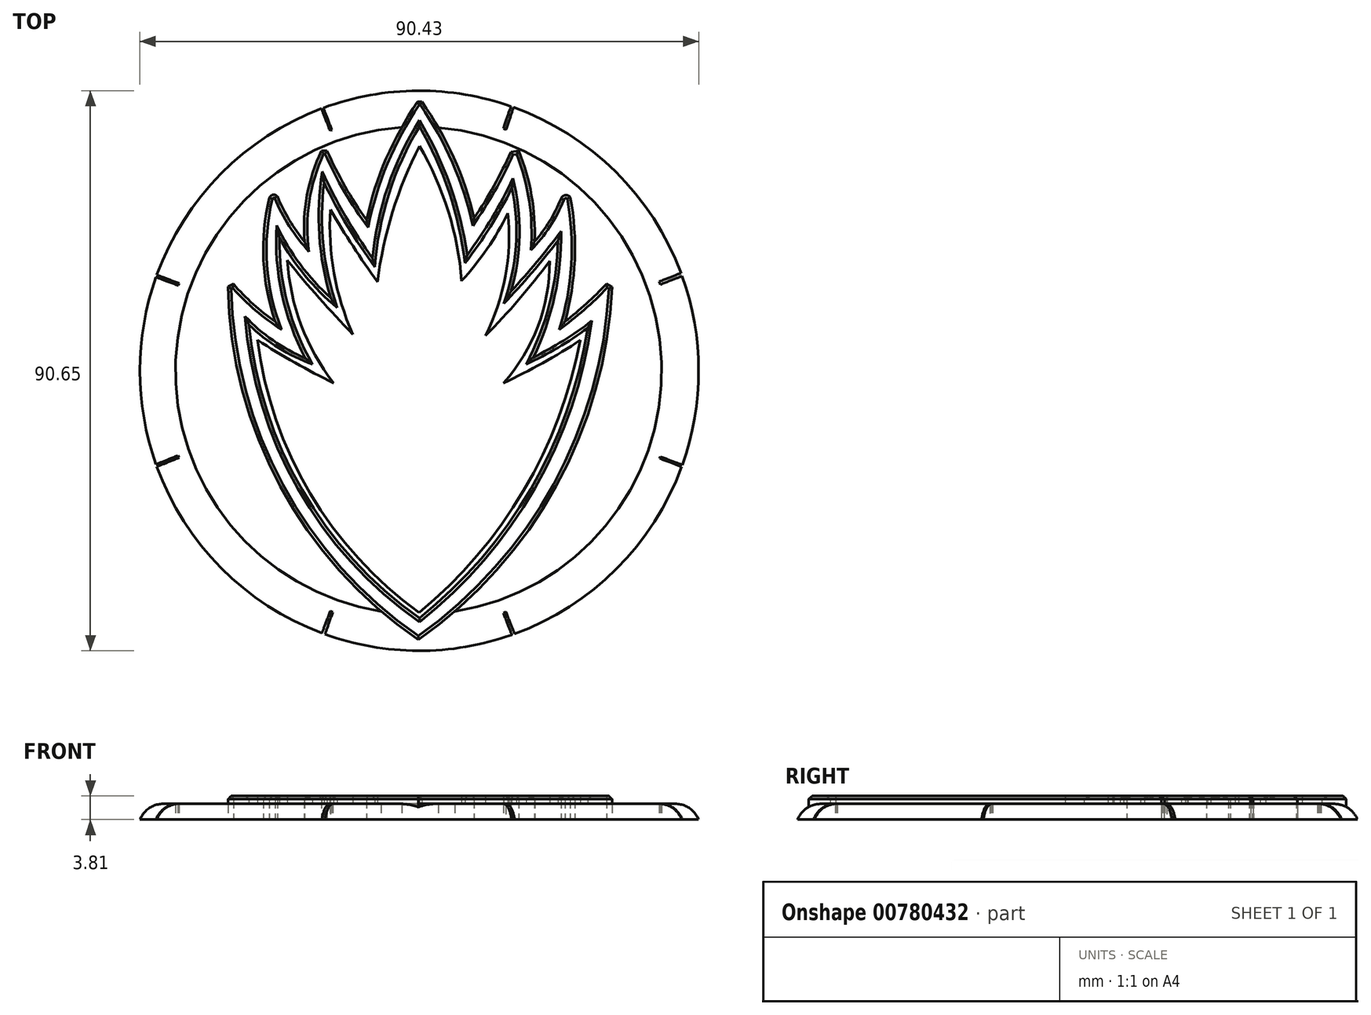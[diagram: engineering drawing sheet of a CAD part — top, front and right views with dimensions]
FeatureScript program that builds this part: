
annotation { "Feature Type Name" : "Feature", "Feature Type Description" : "" }
export const myFeature = defineFeature(function(context is Context, id is Id, definition is map)
    precondition{}
    {
        {
            var Q0;
            Q0=qCreatedBy(makeId("Top.planeOp"),FACE);
            var sketch = newSketch(context, id + "F0", { "sketchPlane" : qUnion([Q0])});
            skArc(sketch, "E0", {"start": v(0, 52.17) * mm, "mid": v(-45.04, 6.84) * mm, "end": v(0, -38.48) * mm});
            skArc(sketch, "E1", {"start": v(0, -38.48) * mm, "mid": v(45.39, 6.84) * mm, "end": v(0, 52.17) * mm});
            skArc(sketch, "E2", {"start": v(-2.74, 46.25) * mm, "mid": v(-39.28, 8.22) * mm, "end": v(-5.39, -32.19) * mm});
            skArc(sketch, "E3", {"start": v(-5.39, -32.19) * mm, "mid": v(39.37, 5.56) * mm, "end": v(-2.74, 46.25) * mm});
            skSolve(sketch);
        }
        {
            var Q0;
            Q0=makeQuery(id+"F0.imprint","IMPRINT",FACE,{"disambiguationData":[TD([[makeQuery(id+"F0.imprint","IMPRINT",EDGE,{"derivedFrom":sQuery(id+"F0.wireOp",EDGE,"E0")}),1.0]])]});
            extrude(context, id + "F1", {"entities" : qUnion([Q0]), "depth" : 2.54 * mm, "offsetDistance" : 25.4 * mm});
        }
        {
            var Q0;
            Q0=qCreatedBy(makeId("Top.planeOp"),FACE);
            var sketch = newSketch(context, id + "F2", { "sketchPlane" : qUnion([Q0])});
            skArc(sketch, "E4", {"start": v(0, 50.54) * mm, "mid": v(-5.12, 41.31) * mm, "end": v(-8.37, 31.27) * mm});
            skArc(sketch, "E5", {"start": v(-14.75, 42.44) * mm, "mid": v(-11.86, 36.68) * mm, "end": v(-8.37, 31.27) * mm});
            skLineSegment(sketch, "E6", {"start": v(-14.75, 42.44) * mm, "end": v(-15.64, 42.44) * mm});
            skArc(sketch, "E7", {"start": v(-15.64, 42.44) * mm, "mid": v(-18, 35.25) * mm, "end": v(-18.38, 27.7) * mm});
            skArc(sketch, "E8", {"start": v(-22.81, 35.06) * mm, "mid": v(-20.87, 31.21) * mm, "end": v(-18.38, 27.7) * mm});
            skArc(sketch, "E9", {"start": v(-22.81, 35.06) * mm, "mid": v(-23.54, 35.31) * mm, "end": v(-24.1, 34.79) * mm});
            skArc(sketch, "E10", {"start": v(-24.1, 34.79) * mm, "mid": v(-25.04, 24.72) * mm, "end": v(-23.15, 14.8) * mm});
            skArc(sketch, "E11", {"start": v(-29.92, 20.88) * mm, "mid": v(-26.72, 17.63) * mm, "end": v(-23.15, 14.8) * mm});
            skLineSegment(sketch, "E12", {"start": v(-29.92, 20.88) * mm, "end": v(-30.8, 20.45) * mm});
            skArc(sketch, "E13", {"start": v(-30.8, 20.45) * mm, "mid": v(-22.33, -11.86) * mm, "end": v(0, -36.7) * mm});
            skArc(sketch, "E14", {"start": v(0, -36.7) * mm, "mid": v(22.34, -11.8) * mm, "end": v(31.38, 20.41) * mm});
            skLineSegment(sketch, "E15", {"start": v(31.38, 20.41) * mm, "end": v(30.48, 20.92) * mm});
            skArc(sketch, "E16", {"start": v(23.74, 14.81) * mm, "mid": v(27.24, 17.73) * mm, "end": v(30.48, 20.92) * mm});
            skArc(sketch, "E17", {"start": v(23.74, 14.81) * mm, "mid": v(25.33, 24.8) * mm, "end": v(24.61, 34.9) * mm});
            skArc(sketch, "E18", {"start": v(24.61, 34.9) * mm, "mid": v(23.79, 35.25) * mm, "end": v(23.1, 34.66) * mm});
            skArc(sketch, "E19", {"start": v(18.83, 27.75) * mm, "mid": v(21.25, 31.03) * mm, "end": v(23.1, 34.66) * mm});
            skArc(sketch, "E20", {"start": v(18.83, 27.75) * mm, "mid": v(18.34, 35.22) * mm, "end": v(16.27, 42.43) * mm});
            skLineSegment(sketch, "E21", {"start": v(16.27, 42.43) * mm, "end": v(15, 42.26) * mm});
            skArc(sketch, "E22", {"start": v(9.06, 31.57) * mm, "mid": v(12.27, 36.78) * mm, "end": v(15, 42.26) * mm});
            skArc(sketch, "E23", {"start": v(9.06, 31.57) * mm, "mid": v(5.72, 41.37) * mm, "end": v(0.58, 50.35) * mm});
            skLineSegment(sketch, "E24", {"start": v(0.58, 50.35) * mm, "end": v(-0.13, 50.35) * mm});
            skArc(sketch, "E25", {"start": v(0.18, 46.4) * mm, "mid": v(-4.76, 35.45) * mm, "end": v(-7.01, 23.65) * mm});
            skArc(sketch, "E26", {"start": v(-15.25, 37.3) * mm, "mid": v(-11.45, 30.28) * mm, "end": v(-7.01, 23.65) * mm});
            skArc(sketch, "E27", {"start": v(-15.25, 37.3) * mm, "mid": v(-15.35, 27.06) * mm, "end": v(-13.12, 17.06) * mm});
            skArc(sketch, "E28", {"start": v(-22.49, 28.4) * mm, "mid": v(-18.35, 22.27) * mm, "end": v(-13.12, 17.06) * mm});
            skArc(sketch, "E29", {"start": v(-22.49, 28.4) * mm, "mid": v(-21.18, 17.79) * mm, "end": v(-17.13, 7.9) * mm});
            skArc(sketch, "E30", {"start": v(-27.4, 14.3) * mm, "mid": v(-22.6, 10.54) * mm, "end": v(-17.13, 7.9) * mm});
            skArc(sketch, "E31", {"start": v(-27.4, 14.3) * mm, "mid": v(-18.79, -12.45) * mm, "end": v(0.18, -33.18) * mm});
            skArc(sketch, "E32", {"start": v(0.18, -33.18) * mm, "mid": v(18.23, -12.28) * mm, "end": v(27.42, 13.76) * mm});
            skArc(sketch, "E33", {"start": v(17.47, 7.9) * mm, "mid": v(22.6, 10.58) * mm, "end": v(27.42, 13.76) * mm});
            skArc(sketch, "E34", {"start": v(17.47, 7.9) * mm, "mid": v(21.24, 17.6) * mm, "end": v(22.61, 27.92) * mm});
            skArc(sketch, "E35", {"start": v(13.83, 17.72) * mm, "mid": v(18.37, 22.7) * mm, "end": v(22.61, 27.92) * mm});
            skArc(sketch, "E36", {"start": v(13.83, 17.72) * mm, "mid": v(15.8, 26.99) * mm, "end": v(15.16, 36.45) * mm});
            skArc(sketch, "E37", {"start": v(7.58, 24.28) * mm, "mid": v(11.68, 30.17) * mm, "end": v(15.16, 36.45) * mm});
            skArc(sketch, "E38", {"start": v(7.58, 24.28) * mm, "mid": v(5.01, 35.72) * mm, "end": v(0.18, 46.4) * mm});
            skSolve(sketch);
        }
        {
            var Q0;
            Q0 = qSketchRegion(id + "F2", true);
            extrude(context, id + "F3", {"entities" : qUnion([Q0]), "operationType" : NewBodyOperationType.ADD, "depth" : 3.8 * mm, "offsetDistance" : 25.4 * mm});
        }
        {
            var Q0;
            Q0=makeQuery(id+"F2.imprint","IMPRINT",FACE,{"disambiguationData":[TD([[makeQuery(id+"F2.imprint","IMPRINT",EDGE,{"derivedFrom":sQuery(id+"F2.wireOp",EDGE,"E25")}),1.0]])]});
            extrude(context, id + "F4", {"entities" : qUnion([Q0]), "operationType" : NewBodyOperationType.ADD, "depth" : 2.54 * mm, "offsetDistance" : 25.4 * mm});
        }
        {
            var Q0;
            Q0=makeQuery(id+"F1.opExtrude","CAP_EDGE",EDGE,{"disambiguationData":[OSD([sQuery(id+"F0.wireOp",EDGE,"E1")])],"isStart":false});
            var Q1;
            Q1=makeQuery(id+"F1.opExtrude","CAP_EDGE",EDGE,{"disambiguationData":[OSD([sQuery(id+"F0.wireOp",EDGE,"E0")])],"isStart":false});
            fillet(context, id + "F5", {"entities" : qUnion([Q0, Q1]), "radius" : 4.06 * mm, "tangentPropagation" : true, "allowEdgeOverflow" : false});
        }
        {
            var Q0;
            Q0=qCreatedBy(makeId("Top.planeOp"),FACE);
            var sketch = newSketch(context, id + "F6", { "sketchPlane" : qUnion([Q0])});
            skLineSegment(sketch, "E39", {"start": v(-15.76, 49.5) * mm, "end": v(-14.28, 45.72) * mm});
            skLineSegment(sketch, "E40", {"start": v(-14.28, 45.72) * mm, "end": v(-13.98, 45.83) * mm});
            skLineSegment(sketch, "E41", {"start": v(-13.98, 45.83) * mm, "end": v(-15.52, 49.76) * mm});
            skLineSegment(sketch, "E42", {"start": v(-15.52, 49.76) * mm, "end": v(-15.76, 49.5) * mm});
            skLineSegment(sketch, "E43", {"start": v(13.77, 46.06) * mm, "end": v(15.35, 50.63) * mm});
            skLineSegment(sketch, "E44", {"start": v(15.35, 50.63) * mm, "end": v(15.43, 49.44) * mm});
            skLineSegment(sketch, "E45", {"start": v(15.43, 49.44) * mm, "end": v(14.2, 45.85) * mm});
            skLineSegment(sketch, "E46", {"start": v(14.2, 45.85) * mm, "end": v(13.77, 46.06) * mm});
            skLineSegment(sketch, "E47", {"start": v(42.7, 22.72) * mm, "end": v(39, 21.28) * mm});
            skLineSegment(sketch, "E48", {"start": v(39, 21.28) * mm, "end": v(39.19, 20.8) * mm});
            skLineSegment(sketch, "E49", {"start": v(39.19, 20.8) * mm, "end": v(42.96, 22.26) * mm});
            skLineSegment(sketch, "E50", {"start": v(42.96, 22.26) * mm, "end": v(42.7, 22.72) * mm});
            skLineSegment(sketch, "E51", {"start": v(39.18, -7.05) * mm, "end": v(42.96, -8.48) * mm});
            skLineSegment(sketch, "E52", {"start": v(42.96, -8.48) * mm, "end": v(42.85, -8.78) * mm});
            skLineSegment(sketch, "E53", {"start": v(42.85, -8.78) * mm, "end": v(39.06, -7.34) * mm});
            skLineSegment(sketch, "E54", {"start": v(39.06, -7.34) * mm, "end": v(39.18, -7.05) * mm});
            skLineSegment(sketch, "E55", {"start": v(15.15, -35.88) * mm, "end": v(13.77, -32.35) * mm});
            skLineSegment(sketch, "E56", {"start": v(13.77, -32.35) * mm, "end": v(14.2, -32.19) * mm});
            skLineSegment(sketch, "E57", {"start": v(14.2, -32.19) * mm, "end": v(15.72, -36.08) * mm});
            skLineSegment(sketch, "E58", {"start": v(15.72, -36.08) * mm, "end": v(15.32, -36.24) * mm});
            skLineSegment(sketch, "E59", {"start": v(15.32, -36.24) * mm, "end": v(15.15, -35.88) * mm});
            skLineSegment(sketch, "E60", {"start": v(-14.23, -32.04) * mm, "end": v(-15.77, -36.1) * mm});
            skLineSegment(sketch, "E61", {"start": v(-15.77, -36.1) * mm, "end": v(-15.25, -36.24) * mm});
            skLineSegment(sketch, "E62", {"start": v(-15.25, -36.24) * mm, "end": v(-13.82, -32.21) * mm});
            skLineSegment(sketch, "E63", {"start": v(-13.82, -32.21) * mm, "end": v(-14.23, -32.04) * mm});
            skLineSegment(sketch, "E64", {"start": v(-42.57, -8.35) * mm, "end": v(-38.88, -6.88) * mm});
            skLineSegment(sketch, "E65", {"start": v(-38.88, -6.88) * mm, "end": v(-38.74, -7.25) * mm});
            skLineSegment(sketch, "E66", {"start": v(-38.74, -7.25) * mm, "end": v(-42.7, -8.82) * mm});
            skLineSegment(sketch, "E67", {"start": v(-42.7, -8.82) * mm, "end": v(-42.57, -8.35) * mm});
            skLineSegment(sketch, "E68", {"start": v(-42.57, 22.44) * mm, "end": v(-38.74, 20.99) * mm});
            skLineSegment(sketch, "E69", {"start": v(-38.74, 20.99) * mm, "end": v(-38.87, 20.65) * mm});
            skLineSegment(sketch, "E70", {"start": v(-38.87, 20.65) * mm, "end": v(-43.13, 22.26) * mm});
            skLineSegment(sketch, "E71", {"start": v(-43.13, 22.26) * mm, "end": v(-42.57, 22.44) * mm});
            skSolve(sketch);
        }
        {
            var Q0;
            Q0 = qSketchRegion(id + "F6", true);
            extrude(context, id + "F7", {"entities" : qUnion([Q0]), "operationType" : NewBodyOperationType.REMOVE, "depth" : 3.56 * mm, "offsetDistance" : 25.4 * mm});
        }
        {
            var Q0;
            Q0=qCreatedBy(makeId("Top.planeOp"),FACE);
            var sketch = newSketch(context, id + "F8", { "sketchPlane" : qUnion([Q0])});
            skArc(sketch, "E72", {"start": v(0.22, 43.22) * mm, "mid": v(-4.16, 32.53) * mm, "end": v(-6.6, 21.23) * mm});
            skArc(sketch, "E73", {"start": v(-14.23, 32.92) * mm, "mid": v(-10.55, 26.98) * mm, "end": v(-6.6, 21.23) * mm});
            skArc(sketch, "E74", {"start": v(-14.23, 32.92) * mm, "mid": v(-13.63, 22.62) * mm, "end": v(-10.6, 12.75) * mm});
            skArc(sketch, "E75", {"start": v(-21.18, 24.71) * mm, "mid": v(-16.02, 18.61) * mm, "end": v(-10.6, 12.75) * mm});
            skArc(sketch, "E76", {"start": v(-21.18, 24.71) * mm, "mid": v(-18.94, 14.22) * mm, "end": v(-13.69, 4.86) * mm});
            skArc(sketch, "E77", {"start": v(-26.01, 11.8) * mm, "mid": v(-19.95, 8.16) * mm, "end": v(-13.69, 4.86) * mm});
            skArc(sketch, "E78", {"start": v(-26.01, 11.8) * mm, "mid": v(-17.52, -12.98) * mm, "end": v(0.16, -32.31) * mm});
            skArc(sketch, "E79", {"start": v(0.16, -32.31) * mm, "mid": v(17.07, -12.53) * mm, "end": v(26.26, 11.8) * mm});
            skArc(sketch, "E80", {"start": v(13.79, 4.86) * mm, "mid": v(20.15, 8.11) * mm, "end": v(26.26, 11.8) * mm});
            skArc(sketch, "E81", {"start": v(13.79, 4.86) * mm, "mid": v(19.38, 14.02) * mm, "end": v(21.27, 24.6) * mm});
            skArc(sketch, "E82", {"start": v(10.88, 12.52) * mm, "mid": v(16.29, 18.38) * mm, "end": v(21.27, 24.6) * mm});
            skArc(sketch, "E83", {"start": v(10.88, 12.52) * mm, "mid": v(14.12, 22.16) * mm, "end": v(14.5, 32.32) * mm});
            skArc(sketch, "E84", {"start": v(7.03, 21.39) * mm, "mid": v(11.16, 26.59) * mm, "end": v(14.5, 32.32) * mm});
            skArc(sketch, "E85", {"start": v(7.03, 21.39) * mm, "mid": v(4.86, 32.69) * mm, "end": v(0.22, 43.22) * mm});
            skSolve(sketch);
        }
        {
            var Q0;
            Q0 = qSketchRegion(id + "F8", true);
            extrude(context, id + "F9", {"entities" : qUnion([Q0]), "operationType" : NewBodyOperationType.ADD, "depth" : 3.8 * mm, "offsetDistance" : 25.4 * mm});
        }
        {
            var Q0;
            Q0=makeQuery(id+"F3.opExtrude","CAP_FACE",FACE,{"disambiguationData":[OSD([sQuery(id+"F2.wireOp",EDGE,"E4"),sQuery(id+"F2.wireOp",EDGE,"E5"),sQuery(id+"F2.wireOp",EDGE,"E6"),sQuery(id+"F2.wireOp",EDGE,"E7"),sQuery(id+"F2.wireOp",EDGE,"E8"),sQuery(id+"F2.wireOp",EDGE,"E9"),sQuery(id+"F2.wireOp",EDGE,"E10"),sQuery(id+"F2.wireOp",EDGE,"E11"),sQuery(id+"F2.wireOp",EDGE,"E12"),sQuery(id+"F2.wireOp",EDGE,"E13"),sQuery(id+"F2.wireOp",EDGE,"E14"),sQuery(id+"F2.wireOp",EDGE,"E15"),sQuery(id+"F2.wireOp",EDGE,"E16"),sQuery(id+"F2.wireOp",EDGE,"E17"),sQuery(id+"F2.wireOp",EDGE,"E18"),sQuery(id+"F2.wireOp",EDGE,"E19"),sQuery(id+"F2.wireOp",EDGE,"E20"),sQuery(id+"F2.wireOp",EDGE,"E21"),sQuery(id+"F2.wireOp",EDGE,"E22"),sQuery(id+"F2.wireOp",EDGE,"E23"),sQuery(id+"F2.wireOp",EDGE,"E24"),sQuery(id+"F2.wireOp",EDGE,"E25"),sQuery(id+"F2.wireOp",EDGE,"E26"),sQuery(id+"F2.wireOp",EDGE,"E27"),sQuery(id+"F2.wireOp",EDGE,"E28"),sQuery(id+"F2.wireOp",EDGE,"E29"),sQuery(id+"F2.wireOp",EDGE,"E30"),sQuery(id+"F2.wireOp",EDGE,"E31"),sQuery(id+"F2.wireOp",EDGE,"E32"),sQuery(id+"F2.wireOp",EDGE,"E33"),sQuery(id+"F2.wireOp",EDGE,"E34"),sQuery(id+"F2.wireOp",EDGE,"E35"),sQuery(id+"F2.wireOp",EDGE,"E36"),sQuery(id+"F2.wireOp",EDGE,"E37"),sQuery(id+"F2.wireOp",EDGE,"E38")])],"isStart":false});
            chamfer(context, id + "F10", {"entities" : qUnion([Q0]), "width" : 0.5 * mm, "tangentPropagation" : true});
        }
    });
